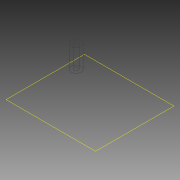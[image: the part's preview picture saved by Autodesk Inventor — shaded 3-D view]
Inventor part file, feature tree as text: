
AUTODESK INVENTOR PART (.ipt)
format: ipt  version: 2015 (Build 190159000, 159)  size: 77,312 bytes
history: native  units: mm
features: plane x2, extrude x1
ambient origin geometry x8: Origin, YZ Plane, XZ Plane, XY Plane, X Axis, Y Axis, Z Axis, Center Point
bodies: Solid1 (feature_tree)
feature tree (3):
  plane  "Work Plane1"
  plane  "Work Plane2"
  extrude  "Extrusion1"  Depth=10.0mm
